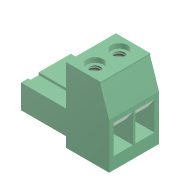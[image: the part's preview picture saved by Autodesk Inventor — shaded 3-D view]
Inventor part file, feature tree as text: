
AUTODESK INVENTOR PART (.ipt)
format: ipt  version: 2022 (Build 260153000, 153)  size: 316,928 bytes
history: native  units: in
note: dims shown in document units (in); Inventor stores cm internally (conversion verified against a paired STEP export)
features: sketch x11, extrude x8, hole x3, plane x3, mirror x1
ambient origin geometry x8: Origin, YZ Plane, XZ Plane, XY Plane, X Axis, Y Axis, Z Axis, Center Point
bodies: Solid1 (feature_tree)
feature tree (26):
  extrude  "Extrusion1"  Depth=0.3701in
  hole  "Hole1"  [1 undecoded]
  extrude  "Extrusion2"  Depth=0.2756in
  extrude  "Extrusion3"  Depth=0.0118in
  extrude  "Extrusion4"  Depth=0.4094in TaperAngle=0.0deg
  extrude  "Extrusion5"  Depth=0.1181in
  extrude  "Extrusion6"  Depth=0.1181in
  plane  "Work Plane2"
  extrude  "Extrusion7"  TaperAngle=0.0deg  [1 undecoded]
  plane  "Work Plane3"
  mirror  "Mirror1"
  hole  "Hole2"  [1 undecoded]
  hole  "Hole3"  [1 undecoded]
  plane  "Work Plane4"
  extrude  "Extrusion8"  Depth=0.0394in
  sketch  "Sketch1"  dims[d0=0.3543in d2=0.3701in]
  sketch  "Sketch2"  dims[d3=0.063in d5=0.2165in]
  sketch  "Sketch3"  dims[d6=0.2362in d7=0.2756in]
  sketch  "Sketch7"  dims[d8=0.0118in d9=0.0079in]
  sketch  "Sketch8"  dims[d10=0.0039in d11=0.4094in d12=0.0in]
  sketch  "Sketch9"  dims[d13=0.6102in d14=0.1181in]
  sketch  "Sketch10"  dims[d15=0.1181in d16=0.2in]
  sketch  "Sketch12"  dims[d17=0.1339in d18=0.0in]
  sketch  "Sketch13"  dims[d19=0.0849in d20=0.224in d21=0.1378in d22=0.0394in d23=90.0deg d24=0.349in d25=0.0in d27=0.1047in]
  sketch  "Sketch14"  dims[d28=0.1181in d29=0.1181in]
  sketch  "Sketch16"  dims[d30=0.1047in d31=0.1047in d32=0.1083in d33=0.1083in d34=0.0394in d35=0.0in d36=0.0591in d37=0.0197in d38=0.0591in d39=0.0197in d40=0.1181in d41=0.0197in d42=0.1457in d43=0.3701in d44=0.0in d45=0.2461in d46=0.2461in d48=0.0197in d49=0.1969in d50=0.0197in d51=0.1969in d52=0.3701in d53=0.0in d54=0.0197in d55=0.1969in d56=0.0197in d57=0.1969in d58=0.3701in d59=0.0in d62=0.1575in d63=0.1575in d64=0.1in d65=0.1575in d66=0.1575in d67=0.1in d68=0.0374in d69=0.0197in d70=0.3543in d71=0.0in d74=0.0787in d75=0.0551in d76=0.1575in d77=0.0in d78=0.0394in d79=0.172in d80=0.1575in d81=0.0787in d82=90.0deg d83=0.315in d84=0.0in d85=0.0394in d86=0.172in d87=0.1575in d88=0.0787in d89=90.0deg d90=0.315in d91=0.0in d92=-0.2165in d93=0.0591in d94=0.0197in d95=0.0787in d96=0.0079in d97=0.0118in d98=0.1181in d99=0.2461in d100=0.0394in d101=0.0in]
note: 4 required parameter values undecoded (feature->parameter linkage not recoverable at this tier; creation-order binding heuristic only, values carry confidence <= 0.55)
